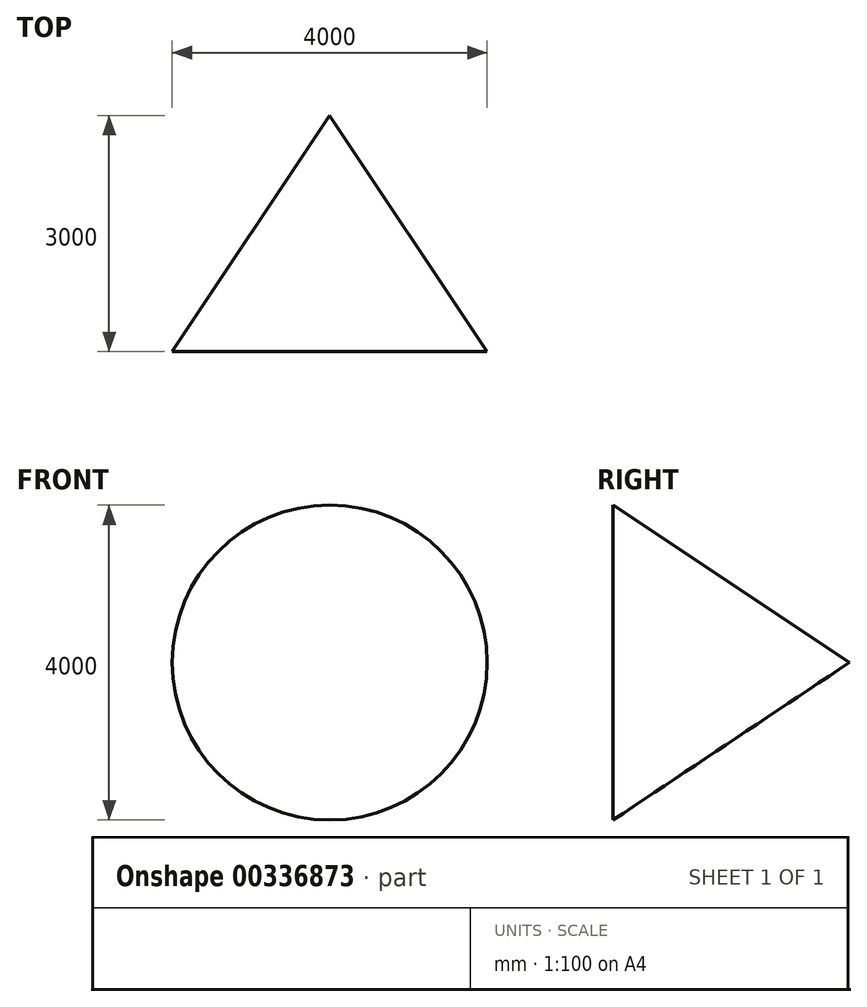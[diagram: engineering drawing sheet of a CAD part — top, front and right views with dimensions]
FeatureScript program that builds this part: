
annotation { "Feature Type Name" : "Feature", "Feature Type Description" : "" }
export const myFeature = defineFeature(function(context is Context, id is Id, definition is map)
    precondition{}
    {
        {
            var Q0;
            Q0=qCreatedBy(makeId("Top.planeOp"),FACE);
            var sketch = newSketch(context, id + "F0", { "sketchPlane" : qUnion([Q0])});
            skLineSegment(sketch, "E0", {"start": v(0, 3000) * mm, "end": v(-2000, 0) * mm});
            skLineSegment(sketch, "E1", {"start": v(-2000, 0) * mm, "end": v(0, 0) * mm});
            skLineSegment(sketch, "E2", {"start": v(0, 0) * mm, "end": v(0, 3000) * mm});
            skSolve(sketch);
        }
        {
            var Q0;
            Q0=makeQuery(id+"F0.imprint","IMPRINT",FACE,{"disambiguationData":[TD([[makeQuery(id+"F0.imprint","IMPRINT",EDGE,{"derivedFrom":sQuery(id+"F0.wireOp",EDGE,"E0")}),1.0]])]});
            var Q1;
            Q1=sQuery(id+"F0.wireOp",EDGE,"E2");
            revolve(context, id + "F1", {"entities" : qUnion([Q0]), "axis" : qUnion([Q1]), "revolveType" : RevolveType.FULL});
        }
    });
